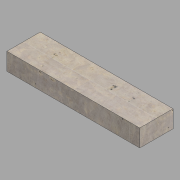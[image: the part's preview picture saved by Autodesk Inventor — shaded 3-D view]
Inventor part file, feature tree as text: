
AUTODESK INVENTOR PART (.ipt)
format: ipt  version: 2022 (Build 260153000, 153)  size: 115,200 bytes
history: native  units: in
note: dims shown in document units (in); Inventor stores cm internally (conversion verified against a paired STEP export)
features: other x1, extrude x1, sketch x1
ambient origin geometry x8: Origin, YZ Plane, XZ Plane, XY Plane, X Axis, Y Axis, Z Axis, Center Point
bodies: Body1 (feature_tree)
feature tree (3):
  other  "Type 2 paver pedestrian"
  extrude  "Extrusion1"  Depth=6.0in
  sketch  "Sketch1"  dims[d0=23.9062in d1=6.0in d2=3.125in d3=0.0in]
